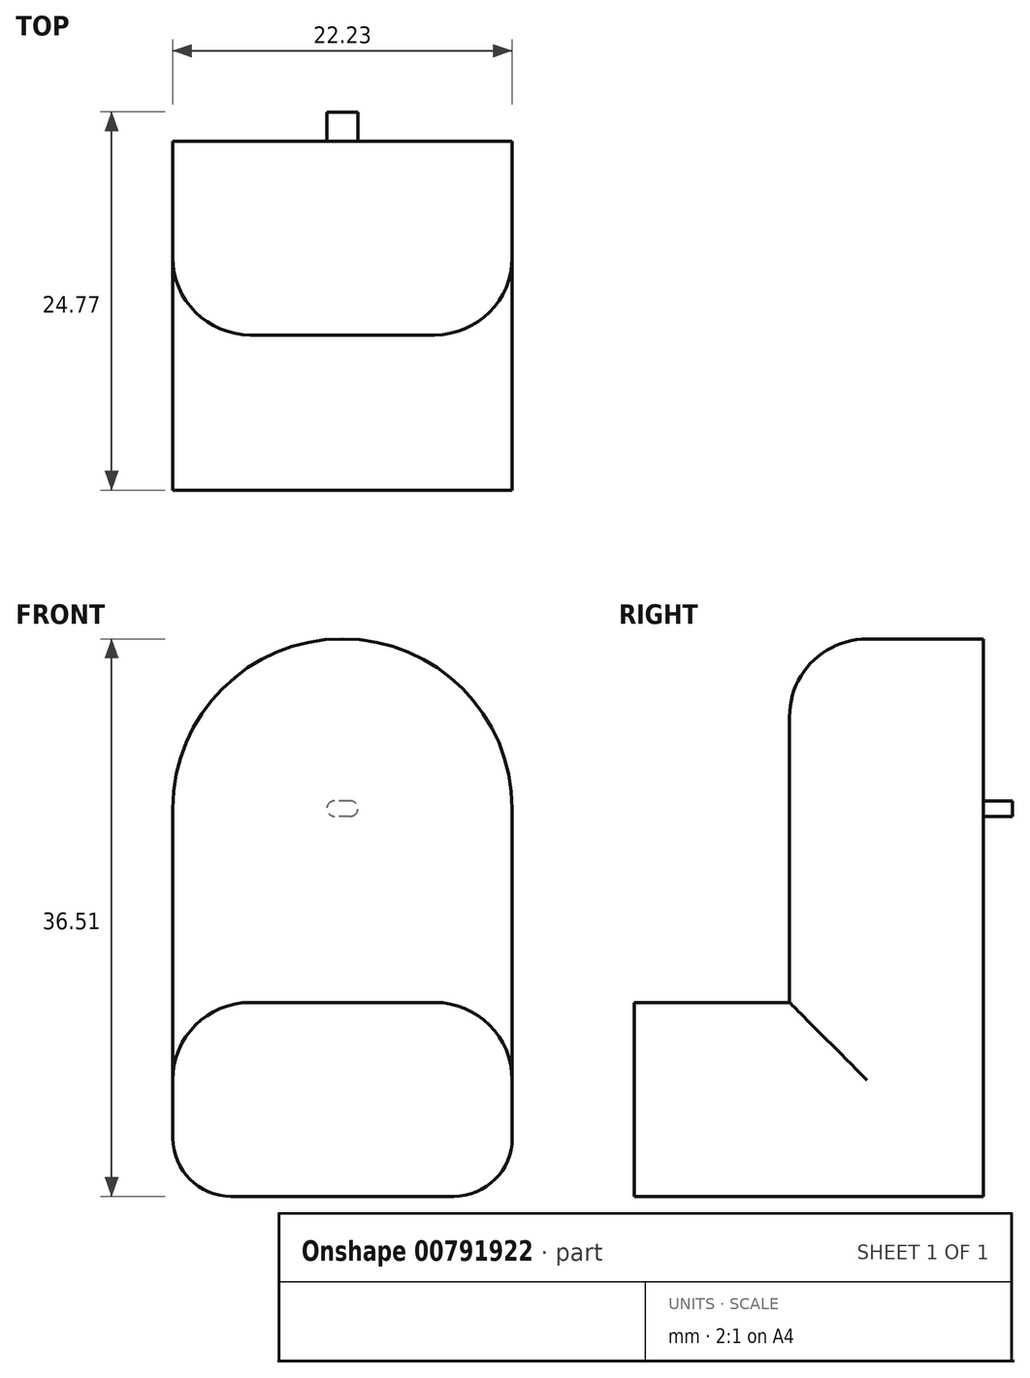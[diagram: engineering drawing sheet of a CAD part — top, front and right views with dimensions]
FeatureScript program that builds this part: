
annotation { "Feature Type Name" : "Feature", "Feature Type Description" : "" }
export const myFeature = defineFeature(function(context is Context, id is Id, definition is map)
    precondition{}
    {
        {
            var Q0;
            Q0=qCreatedBy(makeId("Front.planeOp"),FACE);
            var sketch = newSketch(context, id + "F0", { "sketchPlane" : qUnion([Q0])});
            skLineSegment(sketch, "E0.bottom", {"start": v(-12.77, 14.3) * mm, "end": v(9.46, 14.3) * mm, "construction": true});
            skLineSegment(sketch, "E0.top", {"start": v(-12.77, -11.1) * mm, "end": v(9.46, -11.1) * mm});
            skLineSegment(sketch, "E0.left", {"start": v(-12.77, 14.3) * mm, "end": v(-12.77, -11.1) * mm});
            skLineSegment(sketch, "E0.right", {"start": v(9.46, 14.3) * mm, "end": v(9.46, -11.1) * mm});
            skCircle(sketch, "E1", {"center": v(-1.66, 14.3) * mm, "radius": 11.11 * mm});
            skSolve(sketch);
        }
        {
            var Q0;
            Q0=makeQuery(id+"F0.imprint","IMPRINT",FACE,{"disambiguationData":[TD([[makeQuery(id+"F0.imprint","IMPRINT",EDGE,{"derivedFrom":sQuery(id+"F0.wireOp",EDGE,"E0.top")}),1.0]])]});
            var Q1;
            {var subQ0=sQuery(id+"F0.wireOp",EDGE,"E1");var subQ1=makeQuery(id+"F0.imprint","INTERSECT",VERTEX,{"derivedFrom":[sQuery(id+"F0.wireOp",EDGE,"E0.left"),subQ0]});Q1=makeQuery(id+"F0.imprint","IMPRINT",FACE,{"disambiguationData":[TD([[makeQuery(id+"F0.imprint","IMPRINT",EDGE,{"disambiguationData":[TD([[subQ1,1.0]])],"derivedFrom":subQ0}),1.0]])]});}
            extrude(context, id + "F1", {"entities" : qUnion([Q0, Q1]), "depth" : 12.7 * mm, "offsetDistance" : 25.4 * mm});
        }
        {
            var Q0;
            Q0=makeQuery(id+"F1.opExtrude","CAP_FACE",FACE,{"disambiguationData":[OSD([sQuery(id+"F0.wireOp",EDGE,"E0.top"),sQuery(id+"F0.wireOp",EDGE,"E0.left"),sQuery(id+"F0.wireOp",EDGE,"E0.right"),sQuery(id+"F0.wireOp",EDGE,"E1")])],"isStart":false});
            var sketch = newSketch(context, id + "F2", { "sketchPlane" : qUnion([Q0])});
            skLineSegment(sketch, "E2", {"start": v(-12.77, -11.1) * mm, "end": v(-12.77, 1.6) * mm});
            skLineSegment(sketch, "E3", {"start": v(-12.77, 1.6) * mm, "end": v(9.46, 1.6) * mm});
            skLineSegment(sketch, "E4", {"start": v(9.46, 1.6) * mm, "end": v(9.46, -11.1) * mm});
            skLineSegment(sketch, "E5", {"start": v(9.46, -11.1) * mm, "end": v(-12.77, -11.1) * mm});
            skSolve(sketch);
        }
        {
            var Q0;
            Q0=makeQuery(id+"F2.imprint","IMPRINT",FACE,{"disambiguationData":[TD([[makeQuery(id+"F2.imprint","IMPRINT",EDGE,{"derivedFrom":sQuery(id+"F2.wireOp",EDGE,"E2")}),1.0]])]});
            extrude(context, id + "F3", {"entities" : qUnion([Q0]), "operationType" : NewBodyOperationType.ADD, "depth" : 10.16 * mm, "offsetDistance" : 25.4 * mm});
        }
        {
            var Q0;
            Q0=makeQuery(id+"F1.opExtrude","CAP_EDGE",EDGE,{"disambiguationData":[OSD([sQuery(id+"F0.wireOp",EDGE,"E0.right")])],"isStart":false});
            var Q1;
            Q1=makeQuery(id+"F3.opExtrude","SWEPT_EDGE",EDGE,{"disambiguationData":[OSD([sQuery(id+"F0.wireOp",EDGE,"E0.left"),sQuery(id+"F2.wireOp",EDGE,"E2"),sQuery(id+"F2.wireOp",EDGE,"E3")])]});
            var Q2;
            Q2=makeQuery(id+"F3.opExtrude","SWEPT_EDGE",EDGE,{"disambiguationData":[OSD([sQuery(id+"F0.wireOp",EDGE,"E0.right"),sQuery(id+"F2.wireOp",EDGE,"E3"),sQuery(id+"F2.wireOp",EDGE,"E4")])]});
            fillet(context, id + "F4", {"entities" : qUnion([Q0, Q1, Q2]), "radius" : 5.08 * mm, "tangentPropagation" : true, "allowEdgeOverflow" : false});
        }
        {
            var Q0;
            Q0=makeQuery(id+"F3.boolean.opBoolean","MERGE",EDGE,{"derivedFrom":[makeQuery(id+"F1.opExtrude","SWEPT_EDGE",EDGE,{"disambiguationData":[OSD([sQuery(id+"F0.wireOp",EDGE,"E0.top"),sQuery(id+"F0.wireOp",EDGE,"E0.left")])]}),makeQuery(id+"F3.opExtrude","SWEPT_EDGE",EDGE,{"disambiguationData":[OSD([sQuery(id+"F2.wireOp",EDGE,"E2"),sQuery(id+"F2.wireOp",EDGE,"E5")])]})]});
            var Q1;
            Q1=makeQuery(id+"F3.boolean.opBoolean","MERGE",EDGE,{"derivedFrom":[makeQuery(id+"F1.opExtrude","SWEPT_EDGE",EDGE,{"disambiguationData":[OSD([sQuery(id+"F0.wireOp",EDGE,"E0.top"),sQuery(id+"F0.wireOp",EDGE,"E0.right")])]}),makeQuery(id+"F3.opExtrude","SWEPT_EDGE",EDGE,{"disambiguationData":[OSD([sQuery(id+"F2.wireOp",EDGE,"E4"),sQuery(id+"F2.wireOp",EDGE,"E5")])]})]});
            fillet(context, id + "F5", {"entities" : qUnion([Q0, Q1]), "radius" : 3.8 * mm, "tangentPropagation" : true, "allowEdgeOverflow" : false});
        }
        {
            var Q0;
            Q0=makeQuery(id+"F1.opExtrude","CAP_FACE",FACE,{"disambiguationData":[OSD([sQuery(id+"F0.wireOp",EDGE,"E0.top"),sQuery(id+"F0.wireOp",EDGE,"E0.left"),sQuery(id+"F0.wireOp",EDGE,"E0.right"),sQuery(id+"F0.wireOp",EDGE,"E1")])],"isStart":true});
            var sketch = newSketch(context, id + "F6", { "sketchPlane" : qUnion([Q0])});
            skPoint(sketch, "E6", {"position": v(1.66, 14.3) * mm});
            skLineSegment(sketch, "E7.bottom", {"start": v(0.64, 14.82) * mm, "end": v(2.67, 14.82) * mm});
            skLineSegment(sketch, "E7.top", {"start": v(0.64, 13.8) * mm, "end": v(2.67, 13.8) * mm});
            skLineSegment(sketch, "E7.left", {"start": v(0.64, 14.82) * mm, "end": v(0.64, 13.8) * mm});
            skLineSegment(sketch, "E7.right", {"start": v(2.67, 14.82) * mm, "end": v(2.67, 13.8) * mm});
            skSolve(sketch);
        }
        {
            var Q0;
            Q0=makeQuery(id+"F6.imprint","IMPRINT",FACE,{"disambiguationData":[TD([[makeQuery(id+"F6.imprint","IMPRINT",EDGE,{"derivedFrom":sQuery(id+"F6.wireOp",EDGE,"E7.bottom")}),-1.0]])]});
            extrude(context, id + "F7", {"entities" : qUnion([Q0]), "operationType" : NewBodyOperationType.ADD, "depth" : 1.9 * mm, "offsetDistance" : 25.4 * mm});
        }
        {
            var Q0;
            Q0=makeQuery(id+"F7.opExtrude","SWEPT_EDGE",EDGE,{"disambiguationData":[OSD([sQuery(id+"F6.wireOp",EDGE,"E7.bottom"),sQuery(id+"F6.wireOp",EDGE,"E7.left")])]});
            var Q1;
            Q1=makeQuery(id+"F7.opExtrude","SWEPT_EDGE",EDGE,{"disambiguationData":[OSD([sQuery(id+"F6.wireOp",EDGE,"E7.top"),sQuery(id+"F6.wireOp",EDGE,"E7.left")])]});
            var Q2;
            Q2=makeQuery(id+"F7.opExtrude","SWEPT_EDGE",EDGE,{"disambiguationData":[OSD([sQuery(id+"F6.wireOp",EDGE,"E7.top"),sQuery(id+"F6.wireOp",EDGE,"E7.right")])]});
            var Q3;
            Q3=makeQuery(id+"F7.opExtrude","SWEPT_EDGE",EDGE,{"disambiguationData":[OSD([sQuery(id+"F6.wireOp",EDGE,"E7.bottom"),sQuery(id+"F6.wireOp",EDGE,"E7.right")])]});
            fillet(context, id + "F8", {"entities" : qUnion([Q0, Q1, Q2, Q3]), "radius" : 0.5 * mm, "tangentPropagation" : true, "allowEdgeOverflow" : false});
        }
    });
